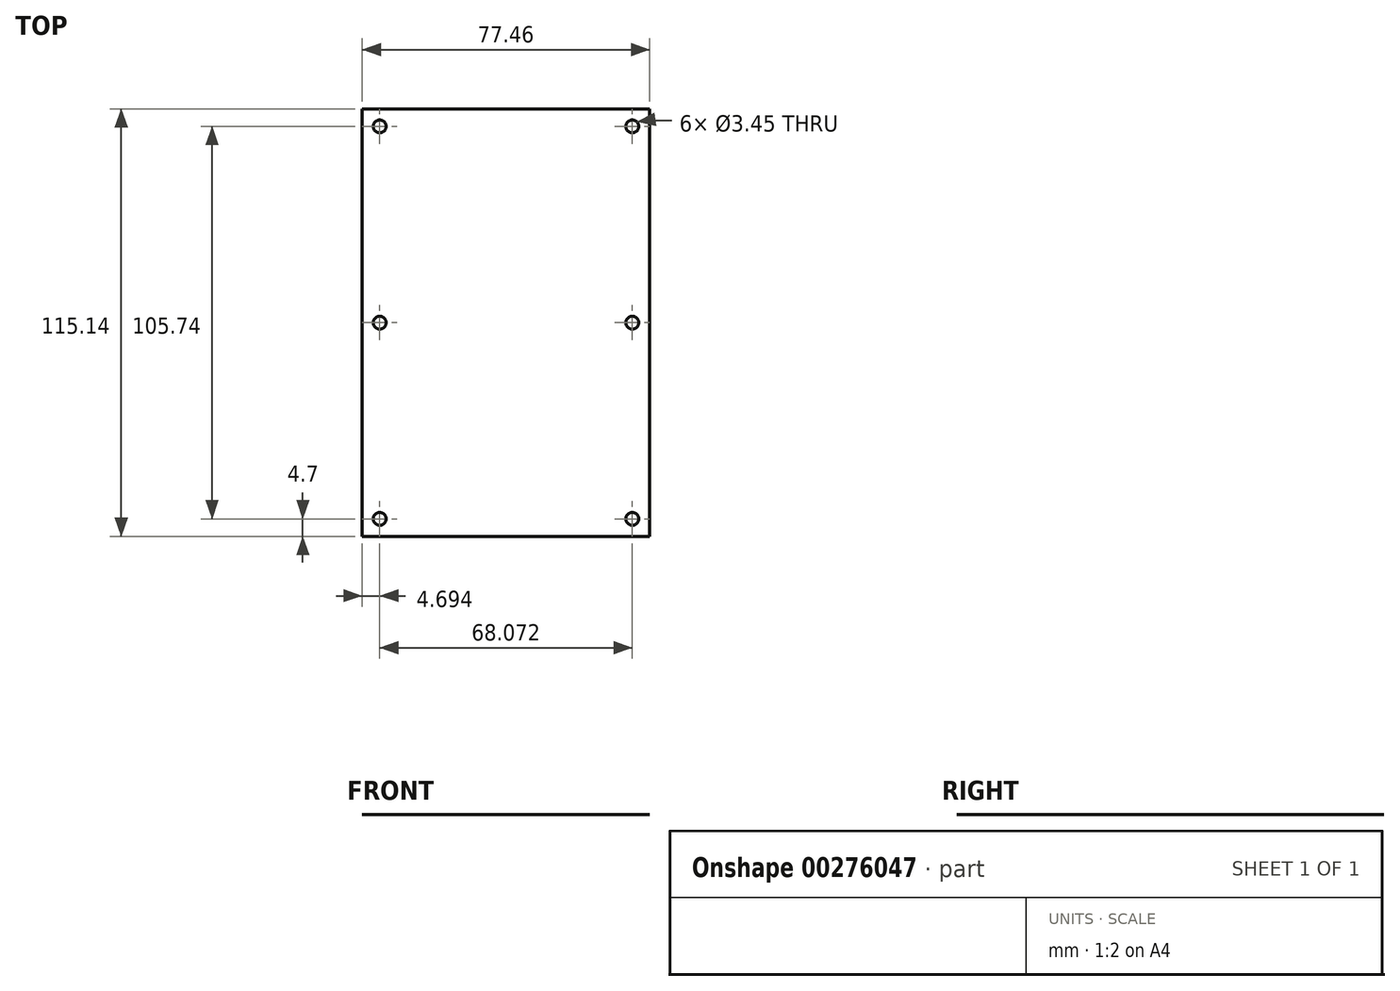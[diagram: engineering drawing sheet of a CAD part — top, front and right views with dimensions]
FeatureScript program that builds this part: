
annotation { "Feature Type Name" : "Feature", "Feature Type Description" : "" }
export const myFeature = defineFeature(function(context is Context, id is Id, definition is map)
    precondition{}
    {
        {
            var Q0;
            Q0=qCreatedBy(makeId("Top.planeOp"),FACE);
            var sketch = newSketch(context, id + "F0", { "sketchPlane" : qUnion([Q0])});
            skLineSegment(sketch, "E0.bottom", {"start": v(-38.73, -57.57) * mm, "end": v(38.74, -57.57) * mm});
            skLineSegment(sketch, "E0.top", {"start": v(-38.74, 57.57) * mm, "end": v(38.73, 57.57) * mm});
            skLineSegment(sketch, "E0.left", {"start": v(-38.73, -57.57) * mm, "end": v(-38.74, 57.57) * mm});
            skLineSegment(sketch, "E0.right", {"start": v(38.74, -57.57) * mm, "end": v(38.73, 57.57) * mm});
            skPoint(sketch, "E0.middle", {"position": v(0, 0) * mm});
            skSolve(sketch);
        }
        {
            var Q0;
            Q0 = qSketchRegion(id + "F0", true);
            extrude(context, id + "F1", {"entities" : qUnion([Q0]), "depth" : 1 / 203.2 * mm});
        }
        {
            var Q0;
            Q0=makeQuery(id+"F1.opExtrude","CAP_FACE",FACE,{"disambiguationData":[OSD([sQuery(id+"F0.wireOp",EDGE,"E0.bottom"),sQuery(id+"F0.wireOp",EDGE,"E0.top"),sQuery(id+"F0.wireOp",EDGE,"E0.left"),sQuery(id+"F0.wireOp",EDGE,"E0.right")])],"isStart":false});
            var sketch = newSketch(context, id + "F2", { "sketchPlane" : qUnion([Q0])});
            skPoint(sketch, "E1", {"position": v(-34.04, 52.87) * mm});
            skPoint(sketch, "E2", {"position": v(34.04, 52.87) * mm});
            skPoint(sketch, "E3", {"position": v(34.04, -52.87) * mm});
            skPoint(sketch, "E4", {"position": v(-34.04, -52.87) * mm});
            skPoint(sketch, "E5", {"position": v(-34.04, 0) * mm});
            skPoint(sketch, "E6", {"position": v(34.04, 0) * mm});
            skSolve(sketch);
        }
        {
            var Q0;
            Q0=sQuery(id+"F2.wireOp",VERTEX,"E1");
            var Q1;
            Q1=sQuery(id+"F2.wireOp",VERTEX,"E2");
            var Q2;
            Q2=sQuery(id+"F2.wireOp",VERTEX,"E3");
            var Q3;
            Q3=sQuery(id+"F2.wireOp",VERTEX,"E4");
            var Q4;
            Q4=sQuery(id+"F2.wireOp",VERTEX,"E5");
            var Q5;
            Q5=sQuery(id+"F2.wireOp",VERTEX,"E6");
            var Q6;
            Q6=makeQuery(id+"F1.opExtrude","SWEPT_BODY",BODY,{"disambiguationData":[OSD([sQuery(id+"F0.wireOp",EDGE,"E0.bottom"),sQuery(id+"F0.wireOp",EDGE,"E0.top"),sQuery(id+"F0.wireOp",EDGE,"E0.left"),sQuery(id+"F0.wireOp",EDGE,"E0.right")])]});
            hole(context, id + "F3", {"style" : HoleStyle.SIMPLE, "endStyle" : HoleEndStyle.THROUGH, "standardTappedOrClearance" : lookupTablePath({ "standard" : "ANSI", "fit" : "Normal (ASME)", "size" : "#5", "type" : "Clearance" }), "standardBlindInLast" : lookupTablePath({ "fit" : "Free", "standard" : "ANSI", "size" : "#5", "type" : "Clearance" }), "holeDiameter" : 3.45 * mm, "tappedDepth" : 4.8 * mm, "tapClearance" : 0, "locations" : qUnion([Q0, Q1, Q2, Q3, Q4, Q5]), "scope" : qUnion([Q6])});
        }
    });
